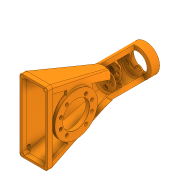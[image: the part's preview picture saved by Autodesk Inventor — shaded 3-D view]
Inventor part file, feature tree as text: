
AUTODESK INVENTOR PART (.ipt)
format: ipt  version: 2020 (Build 240168000, 168)  size: 1,720,320 bytes
history: native  units: in
note: dims shown in document units (in); Inventor stores cm internally (conversion verified against a paired STEP export)
features: sketch x35, extrude x32, projected_geometry x23, chamfer x5, fillet x5, plane x4, loft x2, other x1
ambient origin geometry x8: Origin, YZ Plane, XZ Plane, XY Plane, X Axis, Y Axis, Z Axis, Center Point
bodies: Solid1 (feature_tree)
feature tree (107):
  extrude  "Extrusion1"  Depth=2.0472in
  extrude  "Extrusion2"  Depth=0.5591in
  chamfer  "Chamfer1"  Distance=0.5512in
  extrude  "Extrusion3"  Depth=0.5591in
  extrude  "Extrusion4"  Depth=0.2756in TaperAngle=0.0deg
  extrude  "Extrusion5"  Depth=0.315in
  extrude  "Extrusion6"  Depth=0.4724in
  extrude  "Extrusion7"  Depth=0.0787in
  plane  "Work Plane1"
  sketch  "Sketch9"  dims[d26=0.0984in d27=0.0in d28=0.1575in]
  plane  "Work Plane2"
  extrude  "Extrusion9"  Depth=0.1575in
  sketch  "Sketch11"  dims[d31=15.0deg d32=0.4921in d33=0.0in]
  plane  "Work Plane3"
  extrude  "Extrusion10"  Depth=0.1575in
  extrude  "Extrusion11"  Depth=0.4921in TaperAngle=0.0deg
  loft  "Loft1"
  loft  "Loft2"
  sketch  "Sketch16"  dims[d47=0.315in d48=0.4331in]
  extrude  "Extrusion12"  Depth=0.0787in
  extrude  "Extrusion13"  Depth=0.0984in TaperAngle=0.0deg
  extrude  "Extrusion14"  Depth=0.4331in
  extrude  "Extrusion15"  Depth=0.1575in
  chamfer  "Chamfer23"  Distance=0.0984in
  extrude  "Extrusion19"  Depth=0.8858in
  extrude  "Extrusion20"  Depth=1.6654in
  extrude  "Extrusion21"  TaperAngle=0.0deg  [1 undecoded]
  extrude  "Extrusion22"  Depth=1.6654in
  extrude  "Extrusion23"  Depth=0.1969in
  extrude  "Extrusion24"  Depth=0.3484in
  extrude  "Extrusion25"  Depth=0.1969in
  chamfer  "Chamfer24"  Distance=0.3937in
  extrude  "Extrusion26"  TaperAngle=0.0deg  [1 undecoded]
  fillet  "Fillet2"  [1 undecoded]
  extrude  "Extrusion27"  TaperAngle=0.0deg  [1 undecoded]
  extrude  "Extrusion28"  Depth=0.3937in
  fillet  "Fillet4"  Radius=0.3937in
  fillet  "Fillet5"  Radius=0.7874in
  extrude  "Extrusion29"  Depth=0.8858in
  fillet  "Fillet6"  Radius=1.6654in
  extrude  "Extrusion30"  TaperAngle=0.0deg  [1 undecoded]
  extrude  "Extrusion31"  Depth=0.2224in
  chamfer  "Chamfer26"  Distance=0.0984in
  extrude  "Extrusion32"  Depth=0.0984in
  extrude  "Extrusion33"  Depth=0.0984in TaperAngle=0.0deg
  extrude  "Extrusion34"  Depth=0.0984in
  plane  "Work Plane6"
  extrude  "Extrusion35"  Depth=0.3937in TaperAngle=45.0deg
  extrude  "Extrusion36"  Depth=0.0984in
  chamfer  "Chamfer27"  Distance=0.1969in
  fillet  "Fillet7"  Radius=0.2756in
  sketch  "Sketch1"  dims[d0=2.3622in d1=2.0472in]
  sketch  "Sketch2"  dims[d2=0.5591in d3=0.0in d4=1.6535in d5=0.5512in d6=0.0in]
  sketch  "Sketch3"  dims[d7=0.5591in d8=0.125in d9=0.0137in d10=0.0157in]
  sketch  "Sketch5"  dims[d11=4.7244in d13=360.0deg d15=0.2756in d16=0.0in]
  sketch  "Sketch6"  dims[d17=0.5512in d19=0.315in]
  projected_geometry  "Projected Loop1"
  sketch  "Sketch7"  dims[d20=0.315in d21=0.4724in]
  projected_geometry  "Projected Loop2"
  sketch  "Sketch8"  dims[d22=0.4724in d23=0.0787in d24=0.0787in d25=0.0787in]
  projected_geometry  "Projected Loop3"
  sketch  "Sketch10"  dims[d29=0.1575in d30=1.0994in]
  sketch  "Sketch12"  dims[d34=1.4567in d35=0.0in d36=1.5748in d38=360.0deg]
  sketch  "Sketch13"  dims[d40=0.0787in d41=0.0787in]
  projected_geometry  "Projected Loop4"
  other  "Edges1"
  sketch  "Sketch14"  dims[d42=0.0787in d43=0.0787in]
  projected_geometry  "Projected Loop5"
  sketch  "Sketch15"  dims[d44=0.0787in d45=0.0984in d46=0.0in]
  projected_geometry  "Projected Loop6"
  projected_geometry  "Projected Loop7"
  sketch  "Sketch19"  dims[d51=0.3602in d52=0.1575in]
  projected_geometry  "Projected Loop8"
  sketch  "Sketch20"  dims[d53=0.1575in d54=0.0984in d55=0.0in]
  projected_geometry  "Projected Loop9"
  sketch  "Sketch21"  dims[d56=6.6929in d57=0.8858in]
  sketch  "Sketch25"  dims[d58=1.6654in d59=1.6654in]
  sketch  "Sketch26"  dims[d60=0.0in d61=0.0in]
  projected_geometry  "Projected Loop11"
  sketch  "Sketch27"  dims[d62=1.6654in d63=1.6654in]
  projected_geometry  "Projected Loop12"
  sketch  "Sketch28"  dims[d64=0.1969in d65=0.1969in]
  sketch  "Sketch29"  dims[d66=0.3484in d67=0.3484in]
  sketch  "Sketch30"  dims[d68=0.1969in d69=0.1969in]
  sketch  "Sketch31"  dims[d70=0.1969in d71=0.3937in d72=0.0in]
  projected_geometry  "Projected Loop13"
  projected_geometry  "Projected Loop14"
  sketch  "Sketch33"  dims[d73=0.7874in d74=0.0in d75=0.0in d76=90.0deg d77=0.0in d78=90.0deg]
  projected_geometry  "Projected Loop15"
  sketch  "Sketch34"  dims[d79=0.0in d80=90.0deg d81=0.0in d82=90.0deg]
  sketch  "Sketch35"  dims[d86=0.7874in d87=0.0in d90=0.3937in d91=0.3937in d92=0.7874in d93=0.0in]
  projected_geometry  "Projected Loop16"
  projected_geometry  "Projected Loop17"
  sketch  "Sketch36"  dims[d94=0.1969in d95=0.0in d96=0.8858in d97=1.6654in]
  projected_geometry  "Projected Loop18"
  sketch  "Sketch37"  dims[d98=1.6654in d99=0.0in]
  projected_geometry  "Projected Loop19"
  sketch  "Sketch38"  dims[d100=0.0in d101=0.2224in]
  projected_geometry  "Projected Loop20"
  projected_geometry  "Projected Loop21"
  sketch  "Sketch39"  dims[d102=0.1575in]
  projected_geometry  "Projected Loop22"
  sketch  "Sketch40"  dims[d103=0.1575in]
  sketch  "Sketch41"  dims[d104=0.1575in]
  projected_geometry  "Projected Loop24"
  sketch  "Sketch42"  dims[d105=0.1575in d106=0.0984in d107=0.0984in d108=0.1969in d109=0.0in d193=0.0984in d194=0.3937in d195=0.125in d196=45.0deg d197=0.2756in d198=0.1969in d199=0.0in d200=0.2756in d201=2.7559in d202=0.2756in d203=0.2756in d204=0.2756in d205=0.2756in d206=0.2756in d207=0.2756in d208=0.2756in d209=0.0394in d210=0.2047in d211=0.0in d212=0.1969in d213=0.2756in d214=0.0in d215=1.0in d216=0.0in d217=0.2362in d218=0.2362in d219=0.2362in d220=0.2362in d221=0.2362in d222=0.0in d223=0.3937in d224=0.0in d225=0.1575in d226=0.0in d227=0.315in d228=0.187in d229=0.125in d230=45.0deg d231=1.0in d232=0.0in d233=0.1969in d235=0.4724in d236=0.0984in d237=0.0in d241=0.4724in d243=0.4724in d244=0.4331in d245=0.4724in d247=0.1181in d248=0.0984in d249=0.0in d250=0.0315in d251=0.0394in d252=1.0in d253=0.0in d254=0.315in d255=0.0787in d256=0.0in d257=0.0787in d258=0.0in d259=0.0315in d260=0.0984in d261=0.125in d262=45.0deg d263=0.1181in d264=0.0in d265=0.1181in d266=0.0in d267=0.0394in d268=0.0in d269=0.6299in d270=0.0984in d271=0.0in d272=0.0984in d273=0.0in d274=0.0984in d275=0.125in d276=45.0deg d238=0.5in d239=0.0344in]
  projected_geometry  "Projected Loop25"
note: 5 required parameter values undecoded (feature->parameter linkage not recoverable at this tier; creation-order binding heuristic only, values carry confidence <= 0.55)
